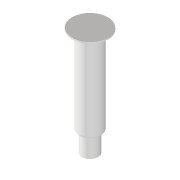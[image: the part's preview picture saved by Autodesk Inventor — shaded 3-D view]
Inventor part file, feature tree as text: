
AUTODESK INVENTOR PART (.ipt)
format: ipt  version: 2022 (Build 260153000, 153)  size: 94,208 bytes
history: native  units: mm
features: revolve x1, sketch x1
ambient origin geometry x8: Origin, YZ Plane, XZ Plane, XY Plane, X Axis, Y Axis, Z Axis, Center Point
bodies: Volumenkörper1 (feature_tree)
feature tree (2):
  revolve  "Umdrehung1"
  sketch  "Skizze1"  dims[d0=5.15mm d1=12.0mm d2=68.3mm d3=7.15mm d4=2.0mm d5=1.0mm d6=90.0deg]
